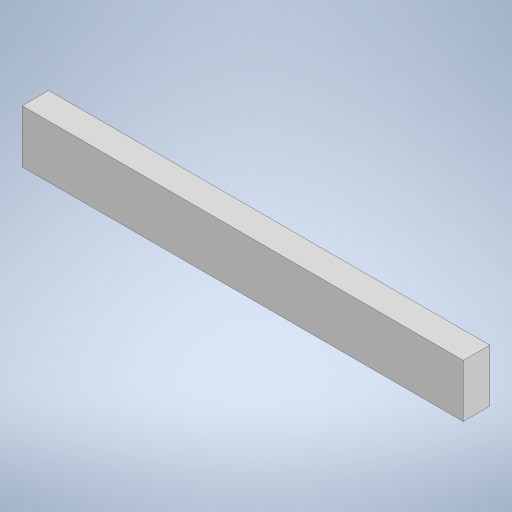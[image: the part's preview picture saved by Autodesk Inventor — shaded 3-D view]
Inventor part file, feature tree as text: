
AUTODESK INVENTOR PART (.ipt)
format: ipt  version: 2023 (Build 270158000, 158)  size: 215,040 bytes
history: native  units: mm
features: other x1, extrude x1, sketch x1
ambient origin geometry x8: Origin, YZ Plane, XZ Plane, XY Plane, X Axis, Y Axis, Z Axis, Center Point
bodies: Body1 (feature_tree)
feature tree (3):
  other  "ソリッド1"
  extrude  "押し出し1"  Depth=30.0mm
  sketch  "スケッチ1"
